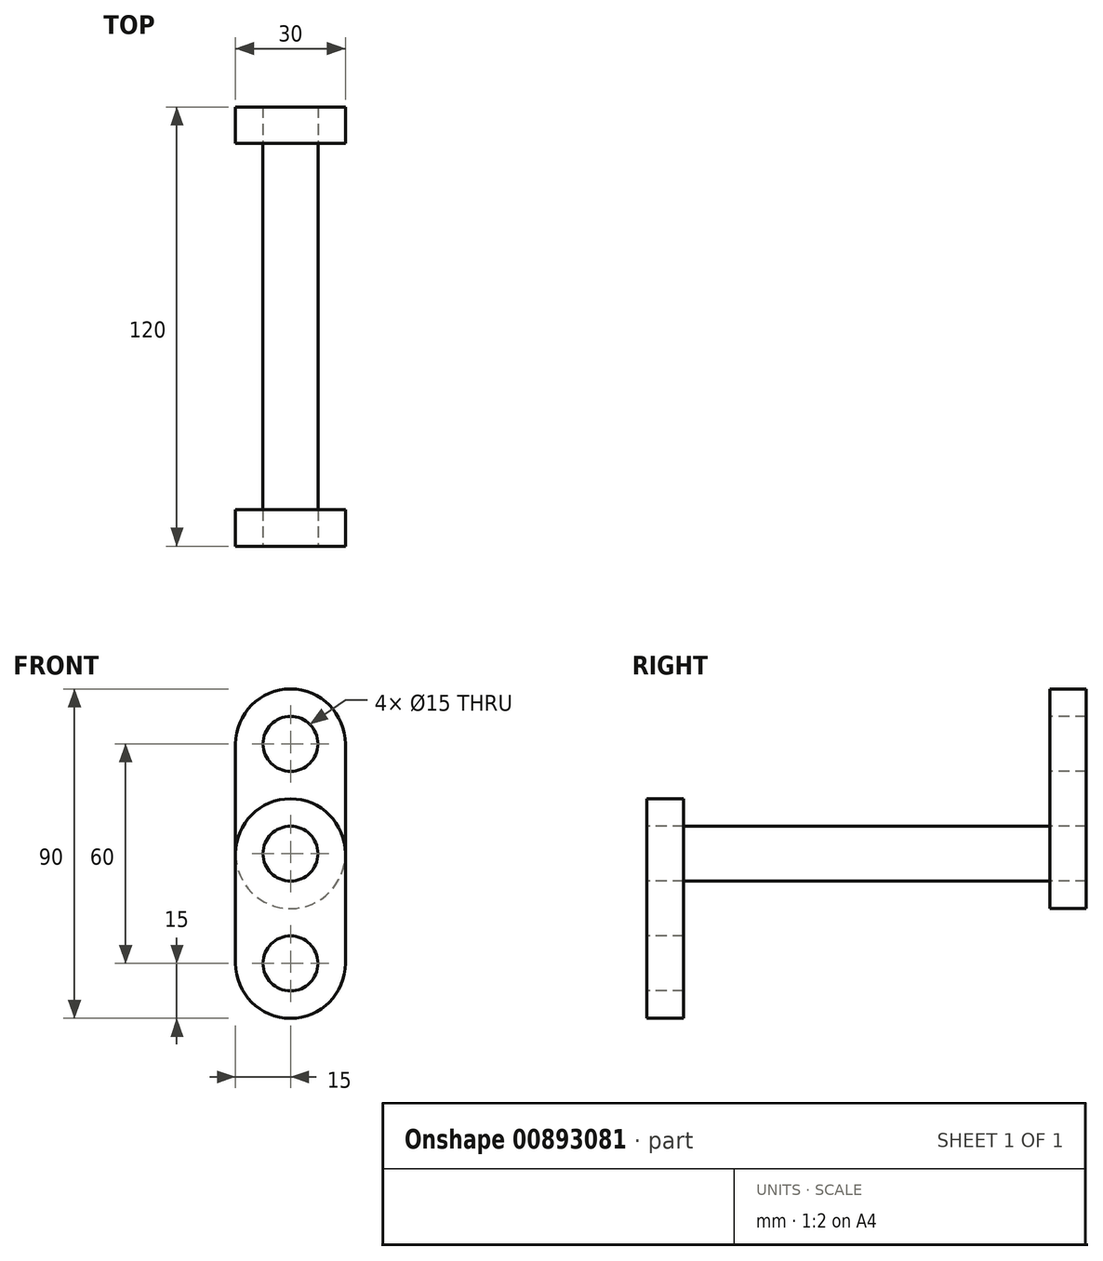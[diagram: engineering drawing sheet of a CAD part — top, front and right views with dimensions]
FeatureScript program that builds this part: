
annotation { "Feature Type Name" : "Feature", "Feature Type Description" : "" }
export const myFeature = defineFeature(function(context is Context, id is Id, definition is map)
    precondition{}
    {
        {
            var Q0;
            Q0=qCreatedBy(makeId("Front.planeOp"),FACE);
            var sketch = newSketch(context, id + "F0", { "sketchPlane" : qUnion([Q0])});
            skArc(sketch, "E0", {"start": v(15, 10) * mm, "mid": v(0, 25) * mm, "end": v(-15, 10) * mm});
            skArc(sketch, "E1", {"start": v(-15, -20) * mm, "mid": v(0, -35) * mm, "end": v(15, -20) * mm});
            skLineSegment(sketch, "E2", {"start": v(-15, 10) * mm, "end": v(-15, -20) * mm});
            skLineSegment(sketch, "E3", {"start": v(15, 10) * mm, "end": v(15, -20) * mm});
            skSolve(sketch);
        }
        {
            var Q0;
            Q0 = qSketchRegion(id + "F0", true);
            extrude(context, id + "F1", {"entities" : qUnion([Q0]), "depth" : 10 * mm, "offsetDistance" : 25 * mm});
        }
        {
            var Q0;
            Q0=makeQuery(id+"F1.opExtrude","CAP_FACE",FACE,{"disambiguationData":[OSD([sQuery(id+"F0.wireOp",EDGE,"E0"),sQuery(id+"F0.wireOp",EDGE,"E1"),sQuery(id+"F0.wireOp",EDGE,"E2"),sQuery(id+"F0.wireOp",EDGE,"E3")])],"isStart":false});
            var sketch = newSketch(context, id + "F2", { "sketchPlane" : qUnion([Q0])});
            skCircle(sketch, "E4", {"center": v(0, 10) * mm, "radius": 7.5 * mm});
            skCircle(sketch, "E5", {"center": v(0, -20) * mm, "radius": 7.5 * mm});
            skSolve(sketch);
        }
        {
            var Q0;
            Q0 = qSketchRegion(id + "F2", true);
            extrude(context, id + "F3", {"entities" : qUnion([Q0]), "operationType" : NewBodyOperationType.REMOVE, "oppositeDirection" : true, "depth" : 25 * mm, "offsetDistance" : 25 * mm});
        }
        {
            var Q0;
            Q0=makeQuery(id+"F1.opExtrude","CAP_FACE",FACE,{"disambiguationData":[OSD([sQuery(id+"F0.wireOp",EDGE,"E0"),sQuery(id+"F0.wireOp",EDGE,"E1"),sQuery(id+"F0.wireOp",EDGE,"E2"),sQuery(id+"F0.wireOp",EDGE,"E3")])],"isStart":true});
            cPlane(context, id + "F4", {"entities" : qUnion([Q0]), "cplaneType" : CPlaneType.OFFSET, "offset" : 100 * mm, "width" : 150 * mm, "height" : 150 * mm});
        }
        {
            var Q0;
            Q0=qCreatedBy(id+"F4.planeOp",FACE);
            var sketch = newSketch(context, id + "F5", { "sketchPlane" : qUnion([Q0])});
            skArc(sketch, "E6", {"start": v(-15, 10) * mm, "mid": v(0, -5) * mm, "end": v(15, 10) * mm});
            skArc(sketch, "E7", {"start": v(15, 40) * mm, "mid": v(0, 55) * mm, "end": v(-15, 40) * mm});
            skLineSegment(sketch, "E8", {"start": v(15, 40) * mm, "end": v(15, 10) * mm});
            skLineSegment(sketch, "E9", {"start": v(-15, 40) * mm, "end": v(-15, 10) * mm});
            skSolve(sketch);
        }
        {
            var Q0;
            Q0 = qSketchRegion(id + "F5", true);
            extrude(context, id + "F6", {"entities" : qUnion([Q0]), "depth" : 10 * mm, "offsetDistance" : 25 * mm});
        }
        {
            var Q0;
            Q0=makeQuery(id+"F6.opExtrude","CAP_FACE",FACE,{"disambiguationData":[OSD([sQuery(id+"F5.wireOp",EDGE,"E6"),sQuery(id+"F5.wireOp",EDGE,"E7"),sQuery(id+"F5.wireOp",EDGE,"E8"),sQuery(id+"F5.wireOp",EDGE,"E9")])],"isStart":true});
            var sketch = newSketch(context, id + "F7", { "sketchPlane" : qUnion([Q0])});
            skCircle(sketch, "E10", {"center": v(0, 10) * mm, "radius": 7.5 * mm});
            skCircle(sketch, "E11", {"center": v(0, 40) * mm, "radius": 7.5 * mm});
            skSolve(sketch);
        }
        {
            var Q0;
            Q0 = qSketchRegion(id + "F7", true);
            extrude(context, id + "F8", {"entities" : qUnion([Q0]), "operationType" : NewBodyOperationType.REMOVE, "oppositeDirection" : true, "depth" : 25 * mm, "offsetDistance" : 25 * mm});
        }
        {
            var Q0;
            Q0=makeQuery(id+"F1.opExtrude","CAP_FACE",FACE,{"disambiguationData":[OSD([sQuery(id+"F0.wireOp",EDGE,"E0"),sQuery(id+"F0.wireOp",EDGE,"E1"),sQuery(id+"F0.wireOp",EDGE,"E2"),sQuery(id+"F0.wireOp",EDGE,"E3")])],"isStart":false});
            var sketch = newSketch(context, id + "F9", { "sketchPlane" : qUnion([Q0])});
            skCircle(sketch, "E12", {"center": v(0, 10) * mm, "radius": 7.5 * mm});
            skSolve(sketch);
        }
        {
            var Q0;
            Q0 = qSketchRegion(id + "F9", true);
            extrude(context, id + "F10", {"entities" : qUnion([Q0]), "oppositeDirection" : true, "depth" : 120 * mm, "offsetDistance" : 25 * mm});
        }
    });
